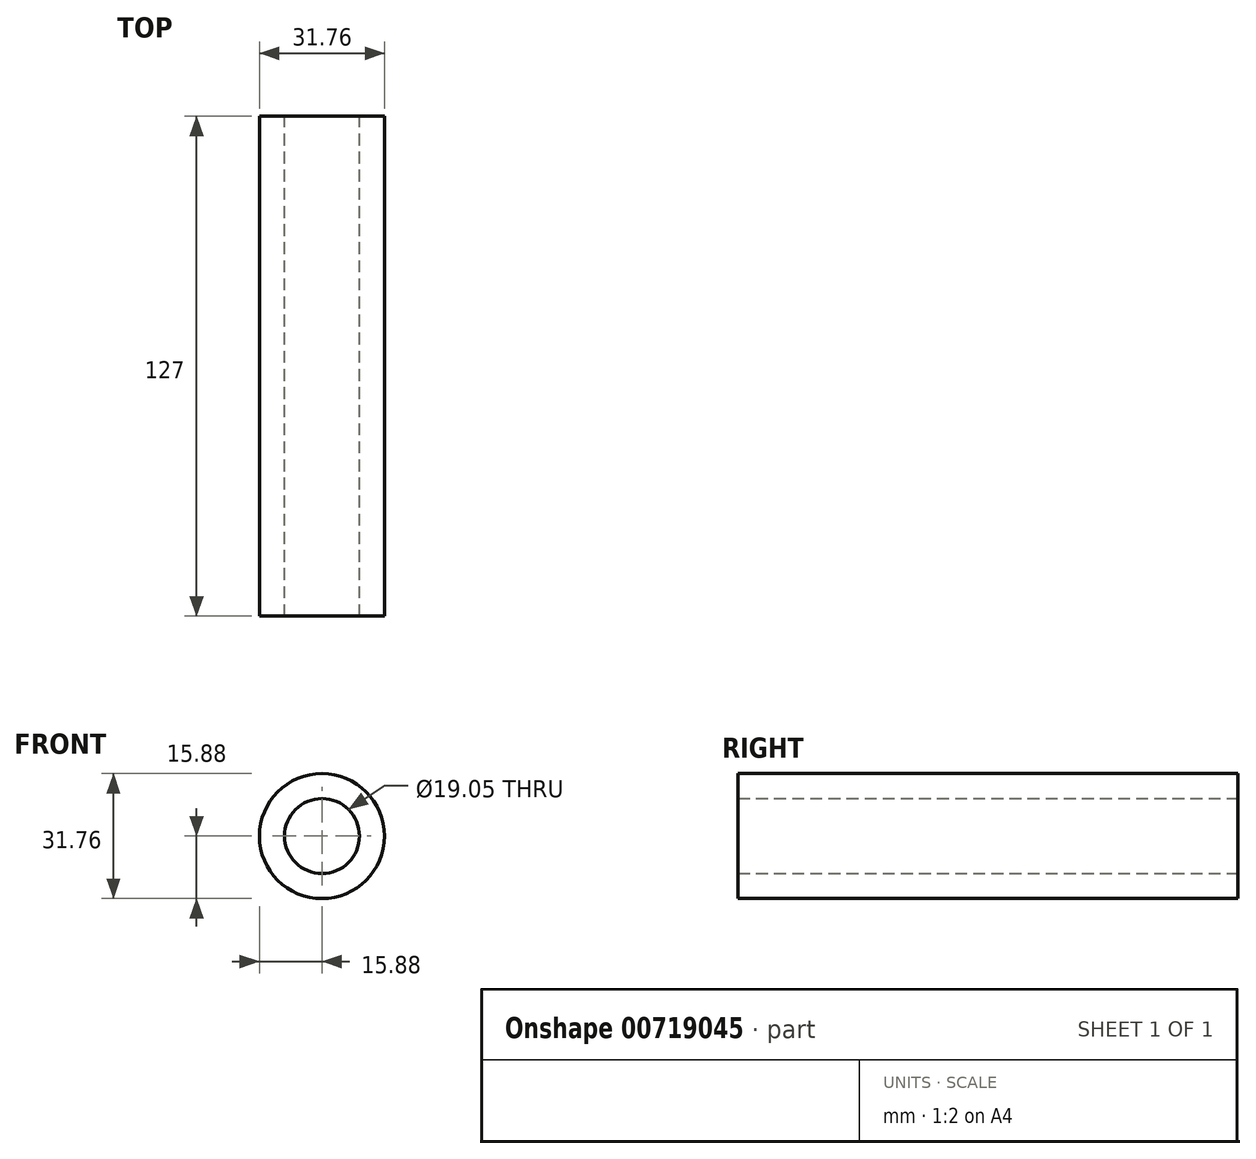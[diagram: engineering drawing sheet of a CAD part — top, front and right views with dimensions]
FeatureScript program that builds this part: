
annotation { "Feature Type Name" : "Feature", "Feature Type Description" : "" }
export const myFeature = defineFeature(function(context is Context, id is Id, definition is map)
    precondition{}
    {
        {
            var Q0;
            Q0=qCreatedBy(makeId("Front.planeOp"),FACE);
            var sketch = newSketch(context, id + "F0", { "sketchPlane" : qUnion([Q0])});
            skCircle(sketch, "E0", {"center": v(0, 0) * mm, "radius": 9.53 * mm});
            skCircle(sketch, "E1", {"center": v(0, 0) * mm, "radius": 15.88 * mm});
            skLineSegment(sketch, "E2", {"start": v(0, 15.88) * mm, "end": v(44.45, 15.88) * mm});
            skLineSegment(sketch, "E3", {"start": v(44.45, 15.88) * mm, "end": v(44.45, -15.88) * mm});
            skLineSegment(sketch, "E4", {"start": v(44.45, -15.88) * mm, "end": v(53.98, -15.88) * mm});
            skLineSegment(sketch, "E5", {"start": v(53.98, -15.88) * mm, "end": v(53.98, 15.88) * mm});
            skLineSegment(sketch, "E6", {"start": v(53.98, 15.88) * mm, "end": v(44.45, 15.88) * mm});
            skLineSegment(sketch, "E7", {"start": v(0, -15.88) * mm, "end": v(44.45, -15.88) * mm});
            skLineSegment(sketch, "E8", {"start": v(15.69, 2.45) * mm, "end": v(44.45, 2.45) * mm});
            skLineSegment(sketch, "E9", {"start": v(15.69, -2.45) * mm, "end": v(44.45, -2.45) * mm});
            skSolve(sketch);
        }
        {
            var Q0;
            Q0=makeQuery(id+"F0.imprint","IMPRINT",FACE,{"disambiguationData":[TD([[makeQuery(id+"F0.imprint","IMPRINT",EDGE,{"derivedFrom":sQuery(id+"F0.wireOp",EDGE,"E0")}),-1.0]])]});
            extrude(context, id + "F1", {"entities" : qUnion([Q0]), "depth" : 127 * mm, "offsetDistance" : 25.4 * mm});
        }
    });
